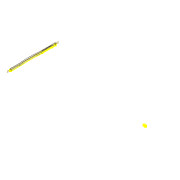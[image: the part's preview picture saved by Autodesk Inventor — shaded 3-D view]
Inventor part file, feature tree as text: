
AUTODESK INVENTOR PART (.ipt)
format: ipt  version: 2022 (Build 260153000, 153)  size: 117,248 bytes
history: native  units: mm
features: sketch x2, extrude x1, projected_geometry x1
ambient origin geometry x8: Origin, YZ Plane, XZ Plane, XY Plane, X Axis, Y Axis, Z Axis, Center Point
bodies: Solid1 (feature_tree)
feature tree (4):
  extrude  "Extrusion1"  Depth=8.0mm
  sketch  "Sketch2"  dims[d2=3.0mm d3=3.0mm d4=8.0mm d5=0.0mm d10=3.0mm d11=19.5mm d12=80.0mm d13=85.0mm d14=220.0mm d15=700.0mm d16=700.0mm]
  sketch  "Sketch1"  dims[d0=270.69mm d1=8.0mm]
  projected_geometry  "Projected Loop1"
